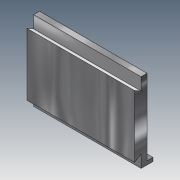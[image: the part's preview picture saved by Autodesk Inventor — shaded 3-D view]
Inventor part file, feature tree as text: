
AUTODESK INVENTOR PART (.ipt)
format: ipt  version: 2018.3 (Build 223284000, 284)  size: 144,384 bytes
history: native  units: in
note: dims shown in document units (in); Inventor stores cm internally (conversion verified against a paired STEP export)
features: extrude x4, sketch x4, mirror x1
ambient origin geometry x8: Origin, YZ Plane, XZ Plane, XY Plane, X Axis, Y Axis, Z Axis, Center Point
bodies: Solid1 (feature_tree)
feature tree (9):
  extrude  "Extrusion1"  Depth=0.24in
  extrude  "Extrusion2"  Depth=0.02in
  mirror  "Mirror1"
  extrude  "Extrusion4"  TaperAngle=60.0deg  [1 undecoded]
  extrude  "Extrusion5"  Depth=0.018in
  sketch  "Sketch1"  dims[d0=0.325in d1=0.24in]
  sketch  "Sketch2"  dims[d2=0.038in d3=0.0in d4=0.02in]
  sketch  "Sketch4"  dims[d5=0.0373in d6=60.0deg]
  sketch  "Sketch5"  dims[d7=0.325in d8=0.0in d15=0.0258in d16=0.0827in d17=0.096in d18=1.0in d19=0.0in d20=0.018in d21=0.218in d22=1.0in d23=0.0in]
note: 1 required parameter value undecoded (feature->parameter linkage not recoverable at this tier; creation-order binding heuristic only, values carry confidence <= 0.55)
